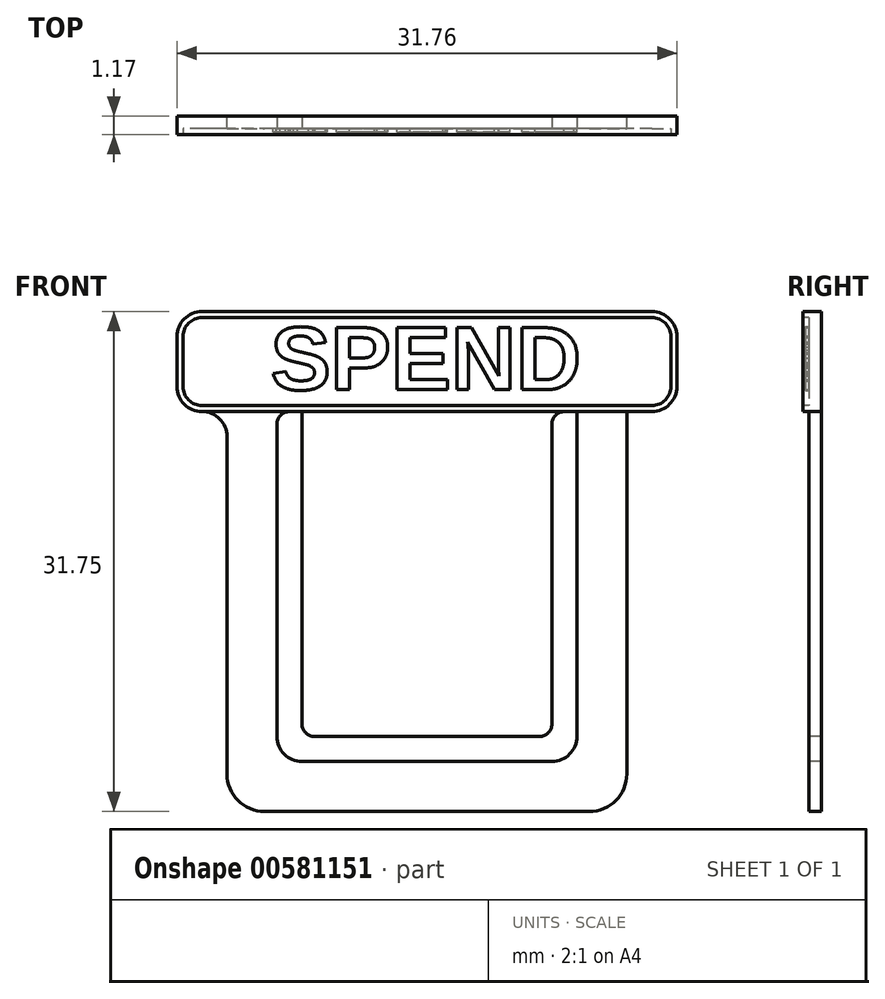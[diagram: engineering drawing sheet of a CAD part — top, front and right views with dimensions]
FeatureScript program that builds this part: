
annotation { "Feature Type Name" : "Feature", "Feature Type Description" : "" }
export const myFeature = defineFeature(function(context is Context, id is Id, definition is map)
    precondition{}
    {
        {
            var Q0;
            Q0=qCreatedBy(makeId("Front.planeOp"),FACE);
            var sketch = newSketch(context, id + "F0", { "sketchPlane" : qUnion([Q0])});
            skLineSegment(sketch, "E0.bottom", {"start": v(12.7, 12.7) * mm, "end": v(-12.7, 12.7) * mm});
            skLineSegment(sketch, "E0.top", {"start": v(12.7, -12.7) * mm, "end": v(-12.7, -12.7) * mm});
            skLineSegment(sketch, "E0.left", {"start": v(12.7, 12.7) * mm, "end": v(12.7, -12.7) * mm});
            skLineSegment(sketch, "E0.right", {"start": v(-12.7, 12.7) * mm, "end": v(-12.7, -12.7) * mm});
            skPoint(sketch, "E0.middle", {"position": v(0, 0) * mm});
            skSolve(sketch);
        }
        {
            var Q0;
            Q0=makeQuery(id+"F0.imprint","IMPRINT",FACE,{"disambiguationData":[TD([[makeQuery(id+"F0.imprint","IMPRINT",EDGE,{"derivedFrom":sQuery(id+"F0.wireOp",EDGE,"E0.bottom")}),1.0]])]});
            extrude(context, id + "F1", {"entities" : qUnion([Q0]), "depth" : 0.8 * mm, "offsetDistance" : 25.4 * mm});
        }
        {
            var Q0;
            Q0=makeQuery(id+"F1.opExtrude","SWEPT_EDGE",EDGE,{"disambiguationData":[OSD([sQuery(id+"F0.wireOp",EDGE,"E0.top"),sQuery(id+"F0.wireOp",EDGE,"E0.left")])]});
            var Q1;
            Q1=makeQuery(id+"F1.opExtrude","SWEPT_EDGE",EDGE,{"disambiguationData":[OSD([sQuery(id+"F0.wireOp",EDGE,"E0.top"),sQuery(id+"F0.wireOp",EDGE,"E0.right")])]});
            fillet(context, id + "F2", {"entities" : qUnion([Q0, Q1]), "radius" : 2.38 * mm, "tangentPropagation" : true, "allowEdgeOverflow" : false});
        }
        {
            var Q0;
            Q0=makeQuery(id+"F1.opExtrude","CAP_FACE",FACE,{"disambiguationData":[OSD([sQuery(id+"F0.wireOp",EDGE,"E0.bottom"),sQuery(id+"F0.wireOp",EDGE,"E0.top"),sQuery(id+"F0.wireOp",EDGE,"E0.left"),sQuery(id+"F0.wireOp",EDGE,"E0.right")])],"isStart":false});
            var sketch = newSketch(context, id + "F3", { "sketchPlane" : qUnion([Q0])});
            skLineSegment(sketch, "E1.bottom", {"start": v(9.52, 12.7) * mm, "end": v(-9.53, 12.7) * mm});
            skLineSegment(sketch, "E1.top", {"start": v(9.53, -9.53) * mm, "end": v(-9.52, -9.53) * mm});
            skLineSegment(sketch, "E1.left", {"start": v(9.52, 12.7) * mm, "end": v(9.53, -9.53) * mm});
            skLineSegment(sketch, "E1.right", {"start": v(-9.53, 12.7) * mm, "end": v(-9.52, -9.53) * mm});
            skPoint(sketch, "E1.middle", {"position": v(0, 0) * mm});
            skSolve(sketch);
        }
        {
            var Q0;
            Q0=makeQuery(id+"F3.imprint","IMPRINT",FACE,{"disambiguationData":[TD([[makeQuery(id+"F3.imprint","IMPRINT",EDGE,{"derivedFrom":sQuery(id+"F3.wireOp",EDGE,"E1.bottom")}),1.0]])]});
            extrude(context, id + "F4", {"entities" : qUnion([Q0]), "operationType" : NewBodyOperationType.REMOVE, "oppositeDirection" : true, "depth" : 4.93 * mm, "offsetDistance" : 25.4 * mm});
        }
        {
            var Q0;
            Q0=makeQuery(id+"F1.opExtrude","CAP_FACE",FACE,{"disambiguationData":[OSD([sQuery(id+"F0.wireOp",EDGE,"E0.bottom"),sQuery(id+"F0.wireOp",EDGE,"E0.top"),sQuery(id+"F0.wireOp",EDGE,"E0.left"),sQuery(id+"F0.wireOp",EDGE,"E0.right")])],"isStart":false});
            var sketch = newSketch(context, id + "F5", { "sketchPlane" : qUnion([Q0])});
            skLineSegment(sketch, "E2.bottom", {"start": v(-15.88, 12.7) * mm, "end": v(15.88, 12.7) * mm});
            skLineSegment(sketch, "E2.top", {"start": v(-15.88, 19.05) * mm, "end": v(15.88, 19.05) * mm});
            skLineSegment(sketch, "E2.left", {"start": v(-15.88, 12.7) * mm, "end": v(-15.88, 19.05) * mm});
            skLineSegment(sketch, "E2.right", {"start": v(15.87, 12.7) * mm, "end": v(15.87, 19.05) * mm});
            skSolve(sketch);
        }
        {
            var Q0;
            Q0=makeQuery(id+"F5.imprint","IMPRINT",FACE,{"disambiguationData":[TD([[makeQuery(id+"F5.imprint","IMPRINT",EDGE,{"derivedFrom":sQuery(id+"F5.wireOp",EDGE,"E2.top")}),-1.0]])]});
            extrude(context, id + "F6", {"entities" : qUnion([Q0]), "operationType" : NewBodyOperationType.ADD, "oppositeDirection" : true, "depth" : 0.8 * mm, "offsetDistance" : 25.4 * mm});
        }
        {
            var Q0;
            Q0=makeQuery(id+"F6.opExtrude","SWEPT_EDGE",EDGE,{"disambiguationData":[OSD([sQuery(id+"F5.wireOp",EDGE,"E2.top"),sQuery(id+"F5.wireOp",EDGE,"E2.left")])]});
            var Q1;
            Q1=makeQuery(id+"F6.opExtrude","SWEPT_EDGE",EDGE,{"disambiguationData":[OSD([sQuery(id+"F5.wireOp",EDGE,"E2.top"),sQuery(id+"F5.wireOp",EDGE,"E2.right")])]});
            var Q2;
            Q2=makeQuery(id+"F6.opExtrude","SWEPT_EDGE",EDGE,{"disambiguationData":[OSD([sQuery(id+"F5.wireOp",EDGE,"E2.bottom"),sQuery(id+"F5.wireOp",EDGE,"E2.right")])]});
            var Q3;
            Q3=makeQuery(id+"F1.opExtrude","SWEPT_EDGE",EDGE,{"disambiguationData":[OSD([sQuery(id+"F0.wireOp",EDGE,"E0.bottom"),sQuery(id+"F0.wireOp",EDGE,"E0.left")])]});
            var Q4;
            Q4=makeQuery(id+"F6.opExtrude","SWEPT_EDGE",EDGE,{"disambiguationData":[OSD([sQuery(id+"F5.wireOp",EDGE,"E2.bottom"),sQuery(id+"F5.wireOp",EDGE,"E2.left")])]});
            var Q5;
            Q5=makeQuery(id+"F1.opExtrude","SWEPT_EDGE",EDGE,{"disambiguationData":[OSD([sQuery(id+"F0.wireOp",EDGE,"E0.bottom"),sQuery(id+"F0.wireOp",EDGE,"E0.right")])]});
            fillet(context, id + "F7", {"entities" : qUnion([Q0, Q1, Q2, Q3, Q4, Q5]), "radius" : 1.59 * mm, "tangentPropagation" : true, "allowEdgeOverflow" : false});
        }
        {
            var Q0;
            Q0=makeQuery(id+"F4.boolean.opBoolean","COPY",EDGE,{"derivedFrom":makeQuery(id+"F4.opExtrude","SWEPT_EDGE",EDGE,{"disambiguationData":[OSD([sQuery(id+"F3.wireOp",EDGE,"E1.top"),sQuery(id+"F3.wireOp",EDGE,"E1.right")])]})});
            var Q1;
            Q1=makeQuery(id+"F4.boolean.opBoolean","COPY",EDGE,{"derivedFrom":makeQuery(id+"F4.opExtrude","SWEPT_EDGE",EDGE,{"disambiguationData":[OSD([sQuery(id+"F3.wireOp",EDGE,"E1.top"),sQuery(id+"F3.wireOp",EDGE,"E1.left")])]})});
            fillet(context, id + "F8", {"entities" : qUnion([Q0, Q1]), "radius" : 1.59 * mm, "tangentPropagation" : true, "allowEdgeOverflow" : false});
        }
        {
            var Q0;
            Q0=makeQuery(id+"F6.boolean.opBoolean","MERGE",FACE,{"derivedFrom":[makeQuery(id+"F1.opExtrude","CAP_FACE",FACE,{"disambiguationData":[OSD([sQuery(id+"F0.wireOp",EDGE,"E0.bottom"),sQuery(id+"F0.wireOp",EDGE,"E0.top"),sQuery(id+"F0.wireOp",EDGE,"E0.left"),sQuery(id+"F0.wireOp",EDGE,"E0.right")])],"isStart":false}),makeQuery(id+"F6.opExtrude","CAP_FACE",FACE,{"disambiguationData":[OSD([sQuery(id+"F5.wireOp",EDGE,"E2.bottom"),sQuery(id+"F5.wireOp",EDGE,"E2.top"),sQuery(id+"F5.wireOp",EDGE,"E2.left"),sQuery(id+"F5.wireOp",EDGE,"E2.right")])],"isStart":true})]});
            var sketch = newSketch(context, id + "F9", { "sketchPlane" : qUnion([Q0])});
            skLineSegment(sketch, "E3.bottom", {"start": v(-7.94, 12.7) * mm, "end": v(7.94, 12.7) * mm});
            skLineSegment(sketch, "E3.top", {"start": v(-7.94, -7.94) * mm, "end": v(7.94, -7.94) * mm});
            skLineSegment(sketch, "E3.left", {"start": v(-7.94, 12.7) * mm, "end": v(-7.94, -7.94) * mm});
            skLineSegment(sketch, "E3.right", {"start": v(7.94, 12.7) * mm, "end": v(7.94, -7.94) * mm});
            skSolve(sketch);
        }
        {
            var Q0;
            Q0=makeQuery(id+"F9.imprint","IMPRINT",FACE,{"disambiguationData":[TD([[makeQuery(id+"F9.imprint","IMPRINT",EDGE,{"derivedFrom":sQuery(id+"F9.wireOp",EDGE,"E3.bottom")}),1.0]])]});
            extrude(context, id + "F10", {"entities" : qUnion([Q0]), "operationType" : NewBodyOperationType.ADD, "oppositeDirection" : true, "depth" : 0.8 * mm, "offsetDistance" : 25.4 * mm});
        }
        {
            var Q0;
            Q0=makeQuery(id+"F10.opExtrude","SWEPT_EDGE",EDGE,{"disambiguationData":[OSD([sQuery(id+"F5.wireOp",EDGE,"E2.bottom"),sQuery(id+"F9.wireOp",EDGE,"E3.bottom"),sQuery(id+"F9.wireOp",EDGE,"E3.left")])]});
            var Q1;
            Q1=makeQuery(id+"F4.boolean.opBoolean","COPY",EDGE,{"derivedFrom":makeQuery(id+"F4.opExtrude","SWEPT_EDGE",EDGE,{"disambiguationData":[OSD([sQuery(id+"F0.wireOp",EDGE,"E0.bottom"),sQuery(id+"F3.wireOp",EDGE,"E1.bottom"),sQuery(id+"F3.wireOp",EDGE,"E1.right")])]})});
            var Q2;
            Q2=makeQuery(id+"F10.opExtrude","SWEPT_EDGE",EDGE,{"disambiguationData":[OSD([sQuery(id+"F5.wireOp",EDGE,"E2.bottom"),sQuery(id+"F9.wireOp",EDGE,"E3.bottom"),sQuery(id+"F9.wireOp",EDGE,"E3.right")])]});
            var Q3;
            Q3=makeQuery(id+"F4.boolean.opBoolean","COPY",EDGE,{"derivedFrom":makeQuery(id+"F4.opExtrude","SWEPT_EDGE",EDGE,{"disambiguationData":[OSD([sQuery(id+"F0.wireOp",EDGE,"E0.bottom"),sQuery(id+"F3.wireOp",EDGE,"E1.bottom"),sQuery(id+"F3.wireOp",EDGE,"E1.left")])]})});
            fillet(context, id + "F11", {"entities" : qUnion([Q0, Q1, Q2, Q3]), "radius" : 0.8 * mm, "tangentPropagation" : true, "allowEdgeOverflow" : false});
        }
        {
            var Q0;
            Q0=makeQuery(id+"F10.opExtrude","SWEPT_EDGE",EDGE,{"disambiguationData":[OSD([sQuery(id+"F9.wireOp",EDGE,"E3.top"),sQuery(id+"F9.wireOp",EDGE,"E3.left")])]});
            var Q1;
            Q1=makeQuery(id+"F10.opExtrude","SWEPT_EDGE",EDGE,{"disambiguationData":[OSD([sQuery(id+"F9.wireOp",EDGE,"E3.top"),sQuery(id+"F9.wireOp",EDGE,"E3.right")])]});
            fillet(context, id + "F12", {"entities" : qUnion([Q0, Q1]), "radius" : 0.8 * mm, "tangentPropagation" : true, "allowEdgeOverflow" : false});
        }
        {
            var Q0;
            Q0=makeQuery(id+"F10.boolean.opBoolean","MERGE",FACE,{"derivedFrom":[makeQuery(id+"F6.boolean.opBoolean","MERGE",FACE,{"derivedFrom":[makeQuery(id+"F1.opExtrude","CAP_FACE",FACE,{"disambiguationData":[OSD([sQuery(id+"F0.wireOp",EDGE,"E0.bottom"),sQuery(id+"F0.wireOp",EDGE,"E0.top"),sQuery(id+"F0.wireOp",EDGE,"E0.left"),sQuery(id+"F0.wireOp",EDGE,"E0.right")])],"isStart":false}),makeQuery(id+"F6.opExtrude","CAP_FACE",FACE,{"disambiguationData":[OSD([sQuery(id+"F5.wireOp",EDGE,"E2.bottom"),sQuery(id+"F5.wireOp",EDGE,"E2.top"),sQuery(id+"F5.wireOp",EDGE,"E2.left"),sQuery(id+"F5.wireOp",EDGE,"E2.right")])],"isStart":true})]}),makeQuery(id+"F10.opExtrude","CAP_FACE",FACE,{"disambiguationData":[OSD([sQuery(id+"F9.wireOp",EDGE,"E3.bottom"),sQuery(id+"F9.wireOp",EDGE,"E3.top"),sQuery(id+"F9.wireOp",EDGE,"E3.left"),sQuery(id+"F9.wireOp",EDGE,"E3.right")])],"isStart":true})]});
            var sketch = newSketch(context, id + "F13", { "sketchPlane" : qUnion([Q0])});
            skArc(sketch, "E4.0", {"start": v(-14.29, 19.05) * mm, "mid": v(-15.41, 18.59) * mm, "end": v(-15.88, 17.46) * mm});
            skLineSegment(sketch, "E5.0", {"start": v(-15.88, 14.29) * mm, "end": v(-15.88, 17.46) * mm});
            skArc(sketch, "E6.0", {"start": v(-15.88, 14.29) * mm, "mid": v(-15.41, 13.16) * mm, "end": v(-14.29, 12.7) * mm});
            skLineSegment(sketch, "E7.0", {"start": v(-14.29, 19.05) * mm, "end": v(14.29, 19.05) * mm});
            skArc(sketch, "E8.0", {"start": v(15.87, 17.46) * mm, "mid": v(15.41, 18.59) * mm, "end": v(14.29, 19.05) * mm});
            skLineSegment(sketch, "E9.0", {"start": v(15.87, 14.29) * mm, "end": v(15.87, 17.46) * mm});
            skArc(sketch, "E10.0", {"start": v(14.29, 12.7) * mm, "mid": v(15.41, 13.16) * mm, "end": v(15.87, 14.29) * mm});
            skLineSegment(sketch, "E11", {"start": v(-14.29, 12.7) * mm, "end": v(14.29, 12.7) * mm});
            skSolve(sketch);
        }
        {
            var Q0;
            Q0=makeQuery(id+"F13.imprint","IMPRINT",FACE,{"disambiguationData":[TD([[makeQuery(id+"F13.imprint","IMPRINT",EDGE,{"derivedFrom":sQuery(id+"F13.wireOp",EDGE,"E4.0")}),1.0]])]});
            extrude(context, id + "F14", {"entities" : qUnion([Q0]), "operationType" : NewBodyOperationType.ADD, "depth" : 0.38 * mm, "offsetDistance" : 25.4 * mm});
        }
        {
            var Q0;
            Q0=makeQuery(id+"F14.opExtrude","CAP_FACE",FACE,{"disambiguationData":[OSD([sQuery(id+"F13.wireOp",EDGE,"E4.0"),sQuery(id+"F13.wireOp",EDGE,"E5.0"),sQuery(id+"F13.wireOp",EDGE,"E6.0"),sQuery(id+"F13.wireOp",EDGE,"E7.0"),sQuery(id+"F13.wireOp",EDGE,"E8.0"),sQuery(id+"F13.wireOp",EDGE,"E9.0"),sQuery(id+"F13.wireOp",EDGE,"E10.0"),sQuery(id+"F13.wireOp",EDGE,"E11")])],"isStart":false});
            var sketch = newSketch(context, id + "F15", { "sketchPlane" : qUnion([Q0])});
            skArc(sketch, "E12.0", {"start": v(-14.29, 19.05) * mm, "mid": v(-15.41, 18.59) * mm, "end": v(-15.88, 17.46) * mm});
            skLineSegment(sketch, "E13.0", {"start": v(-14.29, 19.05) * mm, "end": v(14.29, 19.05) * mm});
            skLineSegment(sketch, "E14.0", {"start": v(-15.88, 14.29) * mm, "end": v(-15.88, 17.46) * mm});
            skArc(sketch, "E15.0", {"start": v(-15.88, 14.29) * mm, "mid": v(-15.41, 13.16) * mm, "end": v(-14.29, 12.7) * mm});
            skLineSegment(sketch, "E16.0", {"start": v(-14.29, 12.7) * mm, "end": v(14.29, 12.7) * mm});
            skArc(sketch, "E17.0", {"start": v(14.29, 12.7) * mm, "mid": v(15.41, 13.16) * mm, "end": v(15.87, 14.29) * mm});
            skArc(sketch, "E18.0", {"start": v(15.87, 17.46) * mm, "mid": v(15.41, 18.59) * mm, "end": v(14.29, 19.05) * mm});
            skArc(sketch, "E19", {"start": v(-14.29, 18.67) * mm, "mid": v(-15.14, 18.32) * mm, "end": v(-15.5, 17.46) * mm});
            skArc(sketch, "E20", {"start": v(-15.5, 14.29) * mm, "mid": v(-15.14, 13.43) * mm, "end": v(-14.29, 13.08) * mm});
            skArc(sketch, "E21", {"start": v(15.5, 17.46) * mm, "mid": v(15.14, 18.32) * mm, "end": v(14.29, 18.67) * mm});
            skArc(sketch, "E22", {"start": v(14.29, 13.08) * mm, "mid": v(15.14, 13.43) * mm, "end": v(15.5, 14.29) * mm});
            skLineSegment(sketch, "E23", {"start": v(-14.29, 19.05) * mm, "end": v(-14.29, 12.7) * mm, "construction": true});
            skLineSegment(sketch, "E24", {"start": v(-15.88, 17.46) * mm, "end": v(15.87, 17.46) * mm, "construction": true});
            skLineSegment(sketch, "E25", {"start": v(14.29, 19.05) * mm, "end": v(14.29, 12.7) * mm, "construction": true});
            skLineSegment(sketch, "E26", {"start": v(15.87, 14.29) * mm, "end": v(-15.88, 14.29) * mm, "construction": true});
            skLineSegment(sketch, "E27", {"start": v(14.29, 18.67) * mm, "end": v(-14.29, 18.67) * mm});
            skLineSegment(sketch, "E28", {"start": v(-15.5, 17.46) * mm, "end": v(-15.5, 14.29) * mm});
            skLineSegment(sketch, "E29", {"start": v(-14.29, 13.08) * mm, "end": v(14.29, 13.08) * mm});
            skLineSegment(sketch, "E30", {"start": v(15.5, 17.46) * mm, "end": v(15.5, 14.29) * mm});
            skSolve(sketch);
        }
        {
            var Q0;
            Q0=makeQuery(id+"F15.imprint","IMPRINT",FACE,{"disambiguationData":[TD([[makeQuery(id+"F15.imprint","IMPRINT",EDGE,{"derivedFrom":sQuery(id+"F15.wireOp",EDGE,"E19")}),1.0]])]});
            var Q1;
            {var subQ0=sQuery(id+"F9.wireOp",EDGE,"E3.right");var subQ1=sQuery(id+"F9.wireOp",EDGE,"E3.top");var subQ3=sQuery(id+"F0.wireOp",EDGE,"E0.bottom");var subQ4=sQuery(id+"F9.wireOp",EDGE,"E3.left");var subQ5=makeQuery(id+"F6.opExtrude","CAP_FACE",FACE,{"disambiguationData":[OSD([sQuery(id+"F5.wireOp",EDGE,"E2.bottom"),sQuery(id+"F5.wireOp",EDGE,"E2.top"),sQuery(id+"F5.wireOp",EDGE,"E2.left"),sQuery(id+"F5.wireOp",EDGE,"E2.right")])],"isStart":true});var subQ6=makeQuery(id+"F1.opExtrude","CAP_FACE",FACE,{"disambiguationData":[OSD([subQ3,sQuery(id+"F0.wireOp",EDGE,"E0.top"),sQuery(id+"F0.wireOp",EDGE,"E0.left"),sQuery(id+"F0.wireOp",EDGE,"E0.right")])],"isStart":false});var subQ7=makeQuery(id+"F10.opExtrude","CAP_FACE",FACE,{"disambiguationData":[OSD([sQuery(id+"F9.wireOp",EDGE,"E3.bottom"),subQ1,subQ4,subQ0])],"isStart":true});Q1=makeQuery(id+"F14.boolean.opBoolean","SPLIT",FACE,{"disambiguationData":[TD([makeQuery(id+"F10.opExtrude","SWEPT_FACE",FACE,{"disambiguationData":[OSD([subQ1])]})])],"derivedFrom":makeQuery(id+"F10.boolean.opBoolean","MERGE",FACE,{"derivedFrom":[makeQuery(id+"F6.boolean.opBoolean","MERGE",FACE,{"derivedFrom":[subQ6,subQ5]}),subQ7]})});}
            extrude(context, id + "F16", {"entities" : qUnion([Q0]), "operationType" : NewBodyOperationType.REMOVE, "endBound" : BoundingType.UP_TO_SURFACE, "oppositeDirection" : true, "depth" : 25.4 * mm, "endBoundEntityFace" : qUnion([Q1]), "offsetDistance" : 25.4 * mm});
        }
        {
            var Q0;
            Q0=qCreatedBy(makeId("Front.planeOp"),FACE);
            var sketch = newSketch(context, id + "F17", { "sketchPlane" : qUnion([Q0])});
            skText(sketch, "E31", { "text": "SPEND", "fontName": "Arimo-Bold.ttf"});
            const initialGuessF17  = {"E31": [-0.00993, 0.01409, 1, 0, 0.00412]};
            skSetInitialGuess(sketch, initialGuessF17);
            skSolve(sketch);
        }
        {
            var Q0;
            Q0 = qSketchRegion(id + "F17", true);
            extrude(context, id + "F18", {"entities" : qUnion([Q0]), "operationType" : NewBodyOperationType.ADD, "depth" : 1.02 * mm, "offsetDistance" : 25.4 * mm});
        }
    });
